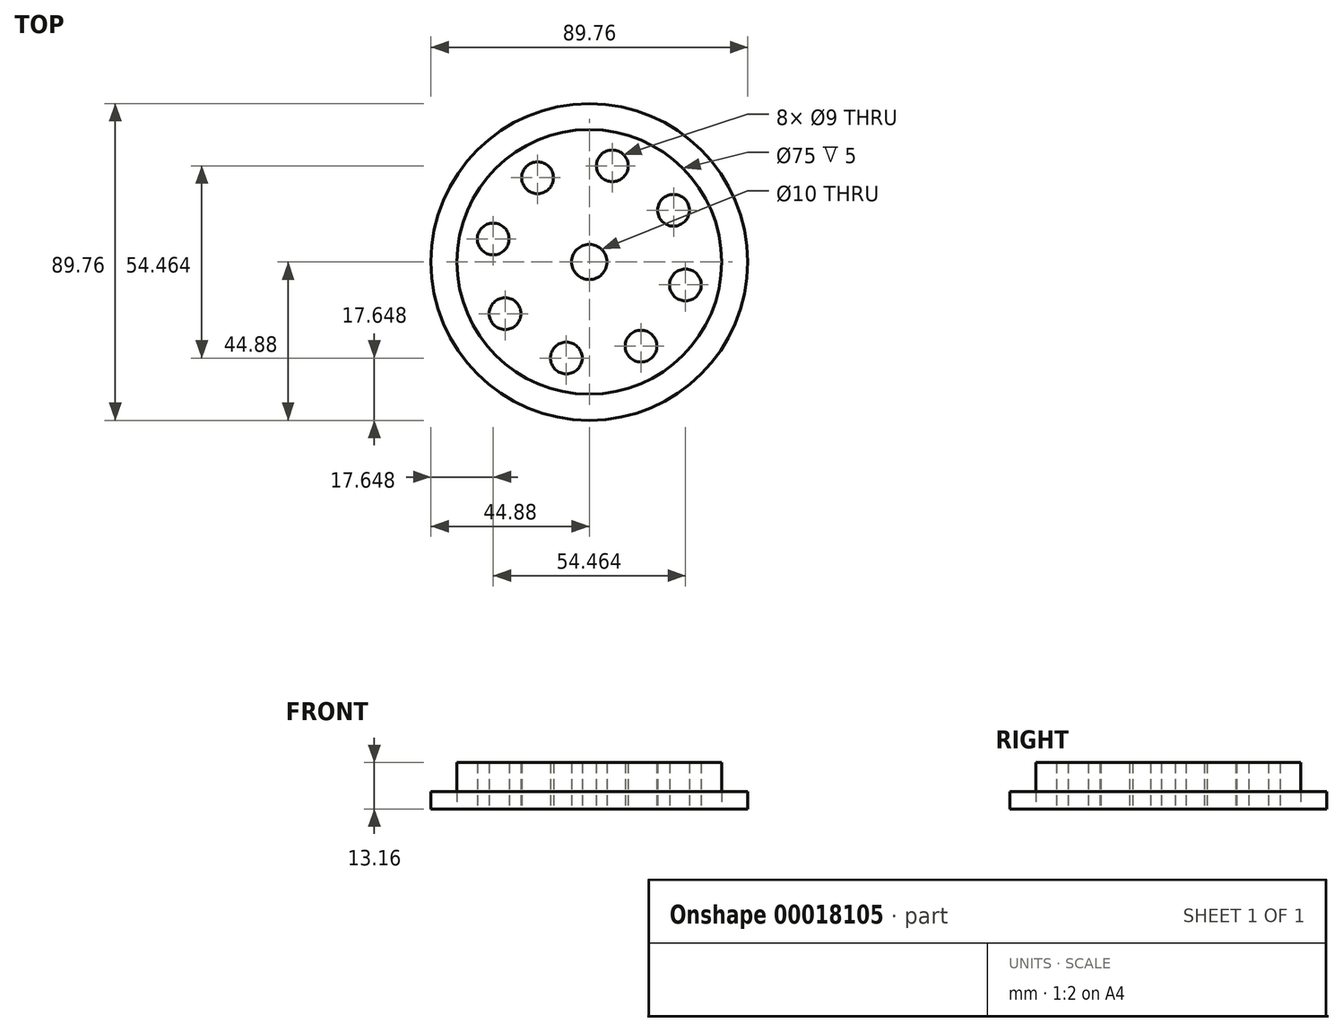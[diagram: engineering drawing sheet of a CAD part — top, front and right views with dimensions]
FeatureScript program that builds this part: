
annotation { "Feature Type Name" : "Feature", "Feature Type Description" : "" }
export const myFeature = defineFeature(function(context is Context, id is Id, definition is map)
    precondition{}
    {
        {
            var Q0;
            Q0=qCreatedBy(makeId("Top.planeOp"),FACE);
            var sketch = newSketch(context, id + "F0", { "sketchPlane" : qUnion([Q0])});
            skCircle(sketch, "E0", {"center": v(0, 0) * mm, "radius": 37.5 * mm});
            skCircle(sketch, "E1.0", {"center": v(0, 0) * mm, "radius": 44.88 * mm});
            skSolve(sketch);
        }
        {
            var Q0;
            Q0=makeQuery(id+"F0.imprint","IMPRINT",FACE,{"disambiguationData":[TD([[makeQuery(id+"F0.imprint","IMPRINT",EDGE,{"derivedFrom":sQuery(id+"F0.wireOp",EDGE,"E0")}),1.0]])]});
            extrude(context, id + "F1", {"entities" : qUnion([Q0]), "depth" : 13.16 * mm});
        }
        {
            var Q0;
            Q0=makeQuery(id+"F0.imprint","IMPRINT",FACE,{"disambiguationData":[TD([[makeQuery(id+"F0.imprint","IMPRINT",EDGE,{"derivedFrom":sQuery(id+"F0.wireOp",EDGE,"E0")}),-1.0]])]});
            extrude(context, id + "F2", {"entities" : qUnion([Q0]), "depth" : 5 * mm});
        }
        {
            var Q0;
            Q0=qCreatedBy(makeId("Top.planeOp"),FACE);
            var sketch = newSketch(context, id + "F3", { "sketchPlane" : qUnion([Q0])});
            skCircle(sketch, "E2", {"center": v(23.86, 14.65) * mm, "radius": 4.5 * mm});
            skCircle(sketch, "E3.1.0", {"center": v(6.51, 27.23) * mm, "radius": 4.5 * mm});
            skCircle(sketch, "E3.2.0", {"center": v(-14.65, 23.86) * mm, "radius": 4.5 * mm});
            skCircle(sketch, "E3.3.0", {"center": v(-27.23, 6.51) * mm, "radius": 4.5 * mm});
            skCircle(sketch, "E3.4.0", {"center": v(-23.86, -14.65) * mm, "radius": 4.5 * mm});
            skCircle(sketch, "E3.5.0", {"center": v(-6.51, -27.23) * mm, "radius": 4.5 * mm});
            skCircle(sketch, "E3.6.0", {"center": v(14.65, -23.86) * mm, "radius": 4.5 * mm});
            skCircle(sketch, "E3.7.0", {"center": v(27.23, -6.51) * mm, "radius": 4.5 * mm});
            skPoint(sketch, "E3.center", {"position": v(0, 0) * mm});
            skCircle(sketch, "E4", {"center": v(23.86, 14.65) * mm, "radius": 12.5 * mm, "construction": true});
            skCircle(sketch, "E5.1.0", {"center": v(6.51, 27.23) * mm, "radius": 12.5 * mm, "construction": true});
            skCircle(sketch, "E5.2.0", {"center": v(-14.65, 23.86) * mm, "radius": 12.5 * mm, "construction": true});
            skCircle(sketch, "E5.3.0", {"center": v(-27.23, 6.51) * mm, "radius": 12.5 * mm, "construction": true});
            skCircle(sketch, "E5.4.0", {"center": v(-23.86, -14.65) * mm, "radius": 12.5 * mm, "construction": true});
            skCircle(sketch, "E5.5.0", {"center": v(-6.51, -27.23) * mm, "radius": 12.5 * mm, "construction": true});
            skCircle(sketch, "E5.6.0", {"center": v(14.65, -23.86) * mm, "radius": 12.5 * mm, "construction": true});
            skCircle(sketch, "E5.7.0", {"center": v(27.23, -6.51) * mm, "radius": 12.5 * mm, "construction": true});
            skCircle(sketch, "E6", {"center": v(0, 0) * mm, "radius": 5 * mm});
            skSolve(sketch);
        }
        {
            var Q0;
            Q0=qSketchRegion(id+"F3",true);
            extrude(context, id + "F4", {"entities" : qUnion([Q0]), "operationType" : NewBodyOperationType.REMOVE, "endBound" : BoundingType.THROUGH_ALL, "depth" : 25 * mm});
        }
    });
